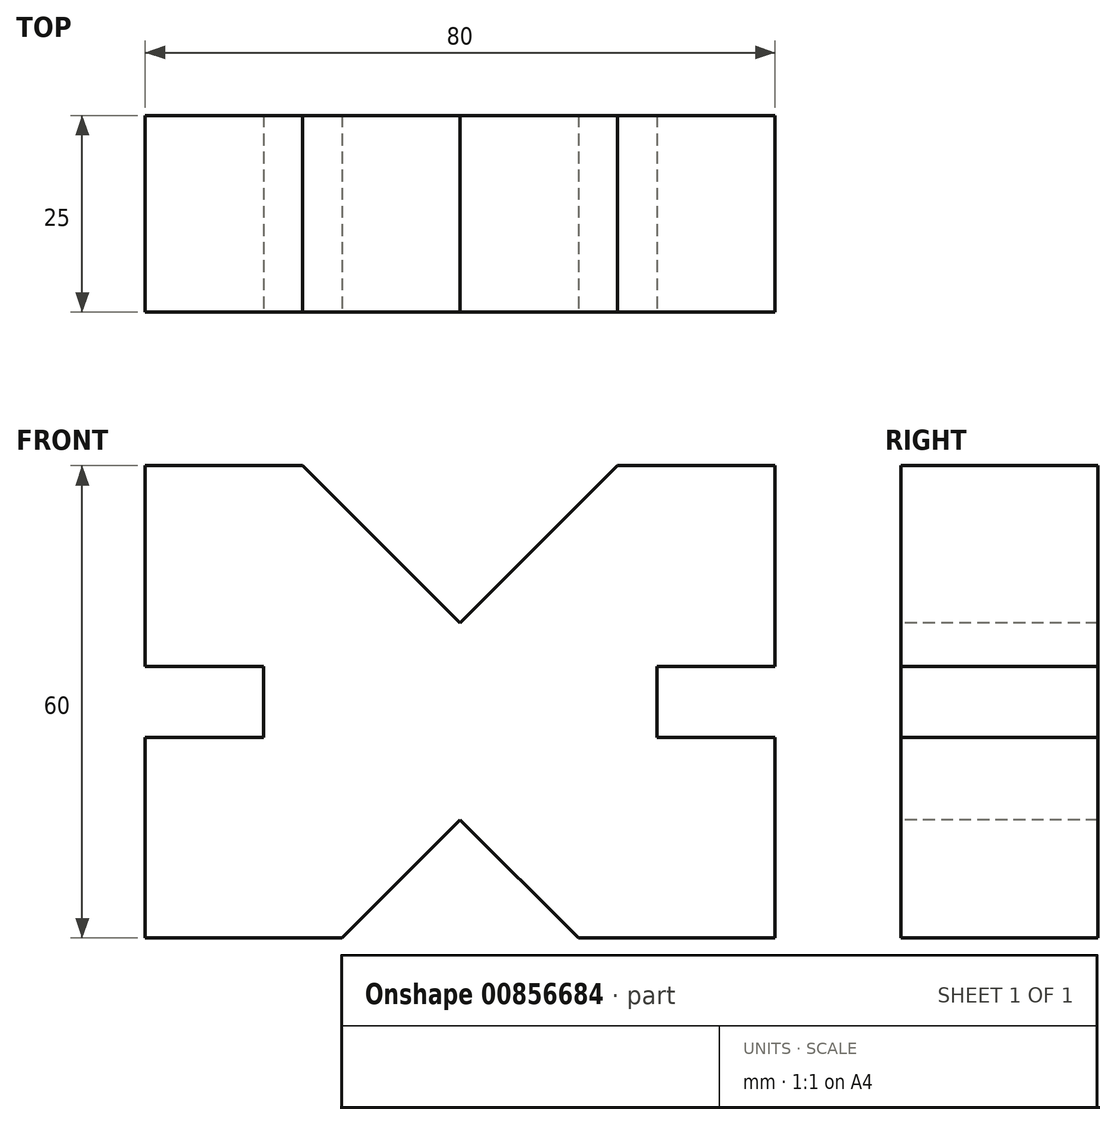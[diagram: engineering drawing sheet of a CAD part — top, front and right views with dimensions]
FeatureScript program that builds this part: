
annotation { "Feature Type Name" : "Feature", "Feature Type Description" : "" }
export const myFeature = defineFeature(function(context is Context, id is Id, definition is map)
    precondition{}
    {
        {
            var Q0;
            Q0=qCreatedBy(makeId("Front.planeOp"),FACE);
            var sketch = newSketch(context, id + "F0", { "sketchPlane" : qUnion([Q0])});
            skLineSegment(sketch, "E0", {"start": v(0, 0) * mm, "end": v(80, 0) * mm});
            skLineSegment(sketch, "E1", {"start": v(80, 0) * mm, "end": v(80, 60) * mm});
            skLineSegment(sketch, "E2", {"start": v(80, 60) * mm, "end": v(0, 60) * mm});
            skLineSegment(sketch, "E3", {"start": v(0, 60) * mm, "end": v(0, 0) * mm});
            skSolve(sketch);
        }
        {
            var Q0;
            Q0=makeQuery(id+"F0.imprint","IMPRINT",FACE,{"disambiguationData":[TD([[makeQuery(id+"F0.imprint","IMPRINT",EDGE,{"derivedFrom":sQuery(id+"F0.wireOp",EDGE,"E0")}),1.0]])]});
            extrude(context, id + "F1", {"entities" : qUnion([Q0]), "endBound" : BoundingType.SYMMETRIC, "depth" : 25 * mm, "offsetDistance" : 25 * mm});
        }
        {
            var Q0;
            Q0=qCreatedBy(makeId("Front.planeOp"),FACE);
            var sketch = newSketch(context, id + "F2", { "sketchPlane" : qUnion([Q0])});
            skLineSegment(sketch, "E4.bottom", {"start": v(0, 34.5) * mm, "end": v(15, 34.5) * mm});
            skLineSegment(sketch, "E4.top", {"start": v(0, 25.5) * mm, "end": v(15, 25.5) * mm});
            skLineSegment(sketch, "E4.left", {"start": v(0, 34.5) * mm, "end": v(0, 25.5) * mm});
            skLineSegment(sketch, "E4.right", {"start": v(15, 34.5) * mm, "end": v(15, 25.5) * mm});
            skLineSegment(sketch, "E5.bottom", {"start": v(80, 34.5) * mm, "end": v(65, 34.5) * mm});
            skLineSegment(sketch, "E5.top", {"start": v(80, 25.5) * mm, "end": v(65, 25.5) * mm});
            skLineSegment(sketch, "E5.left", {"start": v(80, 34.5) * mm, "end": v(80, 25.5) * mm});
            skLineSegment(sketch, "E5.right", {"start": v(65, 34.5) * mm, "end": v(65, 25.5) * mm});
            skLineSegment(sketch, "E6.0.0", {"start": v(60, 60) * mm, "end": v(20, 60) * mm});
            skLineSegment(sketch, "E6.0.2", {"start": v(25, 0) * mm, "end": v(55, 0) * mm});
            skLineSegment(sketch, "E6.0.3", {"start": v(80, 25.5) * mm, "end": v(80, 34.5) * mm});
            skLineSegment(sketch, "E7", {"start": v(20, 60) * mm, "end": v(40, 40) * mm});
            skLineSegment(sketch, "E8", {"start": v(40, 40) * mm, "end": v(60, 60) * mm});
            skLineSegment(sketch, "E9", {"start": v(25, 0) * mm, "end": v(40, 15) * mm});
            skLineSegment(sketch, "E10", {"start": v(40, 15) * mm, "end": v(55, 0) * mm});
            skPoint(sketch, "E11.orphan", {"position": v(0, 60) * mm});
            skPoint(sketch, "E12.orphan", {"position": v(0, 0) * mm});
            skPoint(sketch, "E13.orphan", {"position": v(80, 0) * mm});
            skPoint(sketch, "E14.orphan", {"position": v(80, 60) * mm});
            skSolve(sketch);
        }
        {
            var Q0;
            Q0 = qSketchRegion(id + "F2", true);
            extrude(context, id + "F3", {"entities" : qUnion([Q0]), "operationType" : NewBodyOperationType.REMOVE, "endBound" : BoundingType.THROUGH_ALL, "oppositeDirection" : true, "depth" : 25 * mm, "offsetDistance" : 25 * mm, "hasSecondDirection" : true, "secondDirectionBound" : SecondDirectionBoundingType.THROUGH_ALL, "secondDirectionOppositeDirection" : false, "secondDirectionDepth" : 25 * mm});
        }
    });
